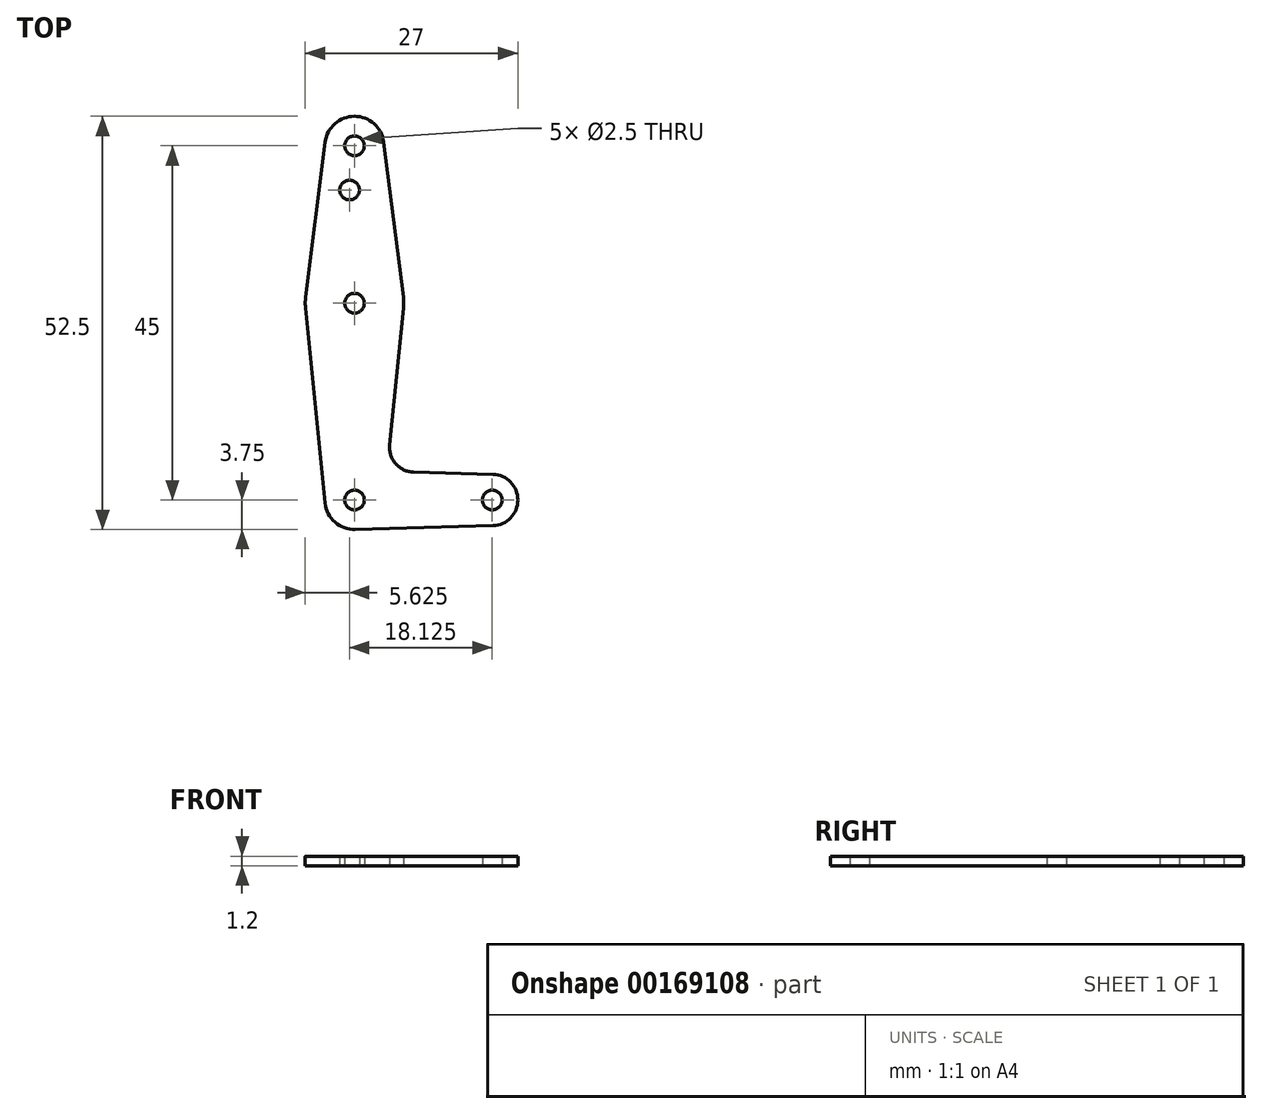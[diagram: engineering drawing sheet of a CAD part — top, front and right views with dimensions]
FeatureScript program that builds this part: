
annotation { "Feature Type Name" : "Feature", "Feature Type Description" : "" }
export const myFeature = defineFeature(function(context is Context, id is Id, definition is map)
    precondition{}
    {
        {
            var Q0;
            Q0=qCreatedBy(makeId("Top.planeOp"),FACE);
            var sketch = newSketch(context, id + "F0", { "sketchPlane" : qUnion([Q0])});
            skLineSegment(sketch, "E0", {"start": v(0, 0) * mm, "end": v(0, 25) * mm, "construction": true});
            skLineSegment(sketch, "E1", {"start": v(0, 25) * mm, "end": v(0, 45) * mm, "construction": true});
            skLineSegment(sketch, "E2", {"start": v(0, 0) * mm, "end": v(17.5, 0) * mm, "construction": true});
            skCircle(sketch, "E3", {"center": v(0, 0) * mm, "radius": 3.75 * mm});
            skCircle(sketch, "E4", {"center": v(0, 25) * mm, "radius": 6.25 * mm});
            skCircle(sketch, "E5", {"center": v(0, 45) * mm, "radius": 3.75 * mm});
            skCircle(sketch, "E6", {"center": v(17.5, 0) * mm, "radius": 3.25 * mm});
            skLineSegment(sketch, "E7", {"start": v(-3.72, 45.47) * mm, "end": v(-6.2, 25.78) * mm});
            skLineSegment(sketch, "E8", {"start": v(3.72, 45.47) * mm, "end": v(6.2, 25.78) * mm});
            skLineSegment(sketch, "E9", {"start": v(-6.22, 24.38) * mm, "end": v(-3.73, -0.38) * mm});
            skLineSegment(sketch, "E10", {"start": v(6.22, 24.38) * mm, "end": v(4.47, 6.98) * mm});
            skLineSegment(sketch, "E11", {"start": v(7.5, 3.54) * mm, "end": v(17.6, 3.25) * mm});
            skLineSegment(sketch, "E12", {"start": v(0.1, -3.75) * mm, "end": v(17.6, -3.25) * mm});
            skCircle(sketch, "E13", {"center": v(0, 45) * mm, "radius": 1.25 * mm});
            skCircle(sketch, "E14", {"center": v(0, 25) * mm, "radius": 1.25 * mm});
            skCircle(sketch, "E15", {"center": v(0, 0) * mm, "radius": 1.25 * mm});
            skCircle(sketch, "E16", {"center": v(17.5, 0) * mm, "radius": 1.25 * mm});
            skCircle(sketch, "E17", {"center": v(-0.63, 39.38) * mm, "radius": 1.25 * mm});
            skPoint(sketch, "E18.newPointB", {"position": v(0.1, 3.75) * mm});
            skArc(sketch, "E18.filletArc", {"start": v(4.47, 6.98) * mm, "mid": v(5.23, 4.6) * mm, "end": v(7.5, 3.54) * mm});
            skSolve(sketch);
        }
        {
            var Q0;
            Q0 = qSketchRegion(id + "F0", true);
            extrude(context, id + "F1", {"entities" : qUnion([Q0]), "depth" : 1.2 * mm});
        }
    });
